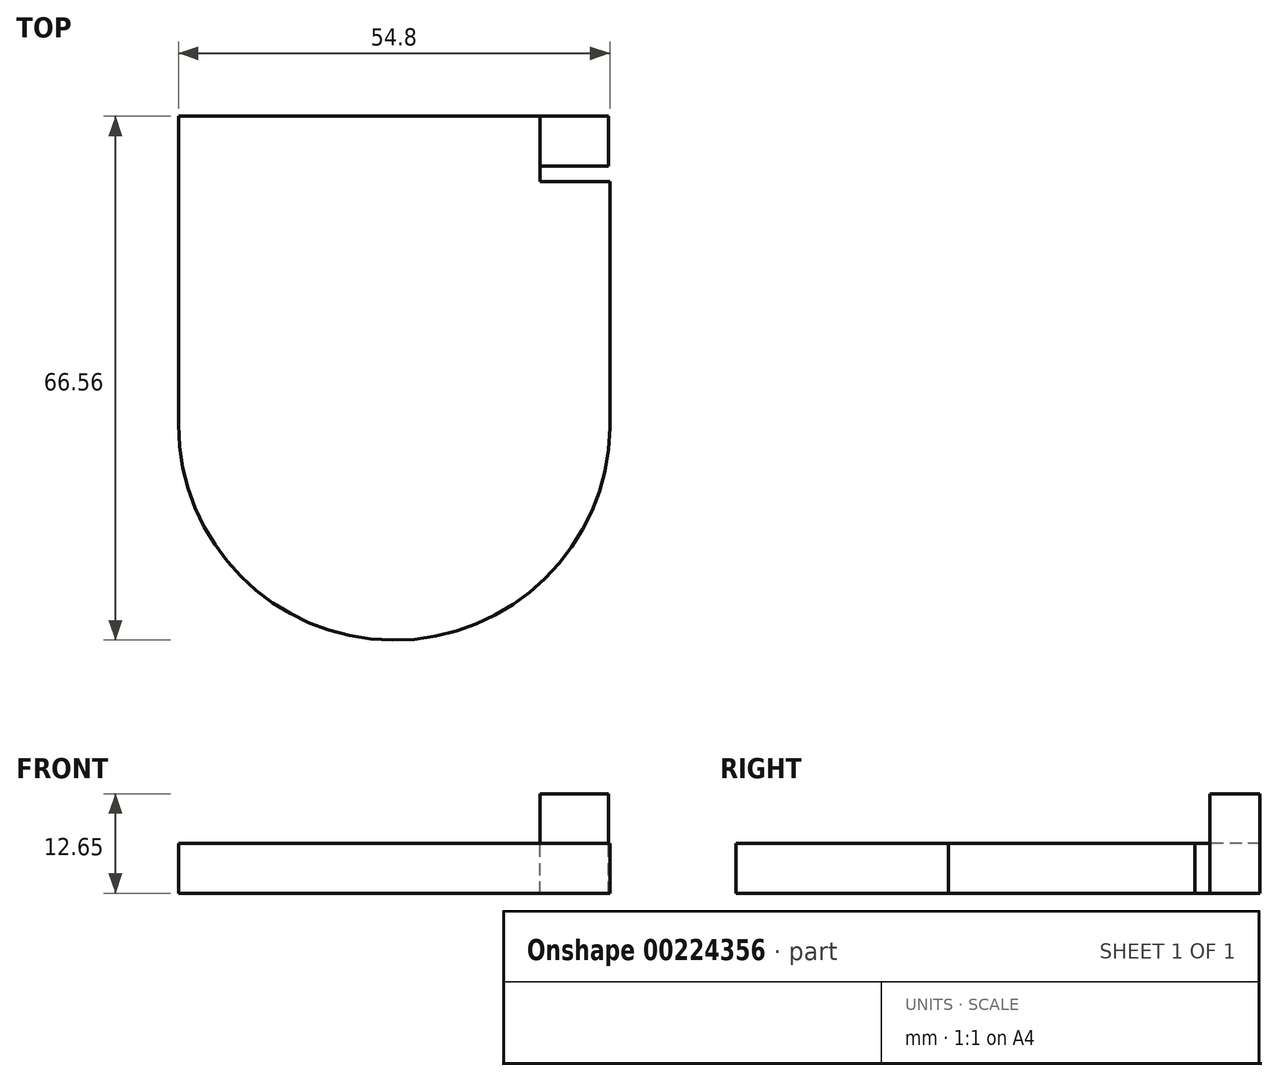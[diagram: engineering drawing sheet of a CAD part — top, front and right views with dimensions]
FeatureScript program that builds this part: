
annotation { "Feature Type Name" : "Feature", "Feature Type Description" : "" }
export const myFeature = defineFeature(function(context is Context, id is Id, definition is map)
    precondition{}
    {
        {
            var Q0;
            Q0=qCreatedBy(makeId("Front.planeOp"),FACE);
            var sketch = newSketch(context, id + "F0", { "sketchPlane" : qUnion([Q0])});
            skLineSegment(sketch, "E0.bottom", {"start": v(0, 0) * mm, "end": v(54.6, 0) * mm});
            skLineSegment(sketch, "E0.top", {"start": v(0, 72.84) * mm, "end": v(19.83, 72.84) * mm});
            skLineSegment(sketch, "E0.left", {"start": v(0, 0) * mm, "end": v(0, 72.84) * mm});
            skLineSegment(sketch, "E0.right", {"start": v(54.6, 0) * mm, "end": v(54.6, 72.84) * mm});
            skLineSegment(sketch, "E1", {"start": v(19.83, 72.84) * mm, "end": v(19.83, 38.56) * mm});
            skLineSegment(sketch, "E2", {"start": v(33.98, 72.84) * mm, "end": v(33.98, 38.56) * mm});
            skArc(sketch, "E3", {"start": v(19.83, 38.56) * mm, "mid": v(26.9, 31.49) * mm, "end": v(33.98, 38.56) * mm});
            skLineSegment(sketch, "E4.trimOffspring", {"start": v(33.98, 72.84) * mm, "end": v(54.6, 72.84) * mm});
            skLineSegment(sketch, "E5.bottom", {"start": v(54.6, 0) * mm, "end": v(45.93, 0) * mm});
            skLineSegment(sketch, "E5.top", {"start": v(54.6, 12.65) * mm, "end": v(45.93, 12.65) * mm});
            skLineSegment(sketch, "E5.left", {"start": v(54.6, 0) * mm, "end": v(54.6, 12.65) * mm});
            skLineSegment(sketch, "E5.right", {"start": v(45.93, 0) * mm, "end": v(45.93, 12.65) * mm});
            skSolve(sketch);
        }
        {
            var Q0;
            Q0=qCreatedBy(makeId("Top.planeOp"),FACE);
            var sketch = newSketch(context, id + "F1", { "sketchPlane" : qUnion([Q0])});
            skLineSegment(sketch, "E6", {"start": v(0, 0) * mm, "end": v(0, -39.16) * mm});
            skLineSegment(sketch, "E7", {"start": v(54.8, -8.27) * mm, "end": v(54.8, -39.56) * mm});
            skArc(sketch, "E8", {"start": v(0, -39.16) * mm, "mid": v(27.2, -66.56) * mm, "end": v(54.8, -39.56) * mm});
            skLineSegment(sketch, "E9.top", {"start": v(54.8, -8.27) * mm, "end": v(45.93, -8.27) * mm});
            skLineSegment(sketch, "E9.right", {"start": v(45.93, 0) * mm, "end": v(45.93, -8.27) * mm});
            skPoint(sketch, "E10.orphan", {"position": v(54.8, 0) * mm});
            skLineSegment(sketch, "E11", {"start": v(0, 0) * mm, "end": v(45.93, 0) * mm});
            skSolve(sketch);
        }
        {
            var Q0;
            Q0=makeQuery(id+"F0.imprint","IMPRINT",FACE,{"disambiguationData":[TD([[makeQuery(id+"F0.imprint","IMPRINT",EDGE,{"derivedFrom":sQuery(id+"F0.wireOp",EDGE,"E0.bottom")}),1.0]])]});
            extrude(context, id + "F2", {"entities" : qUnion([Q0]), "depth" : 6.35 * mm});
        }
        {
            var Q0;
            Q0 = qSketchRegion(id + "F1", true);
            extrude(context, id + "F3", {"entities" : qUnion([Q0]), "depth" : 6.35 * mm});
        }
    });
